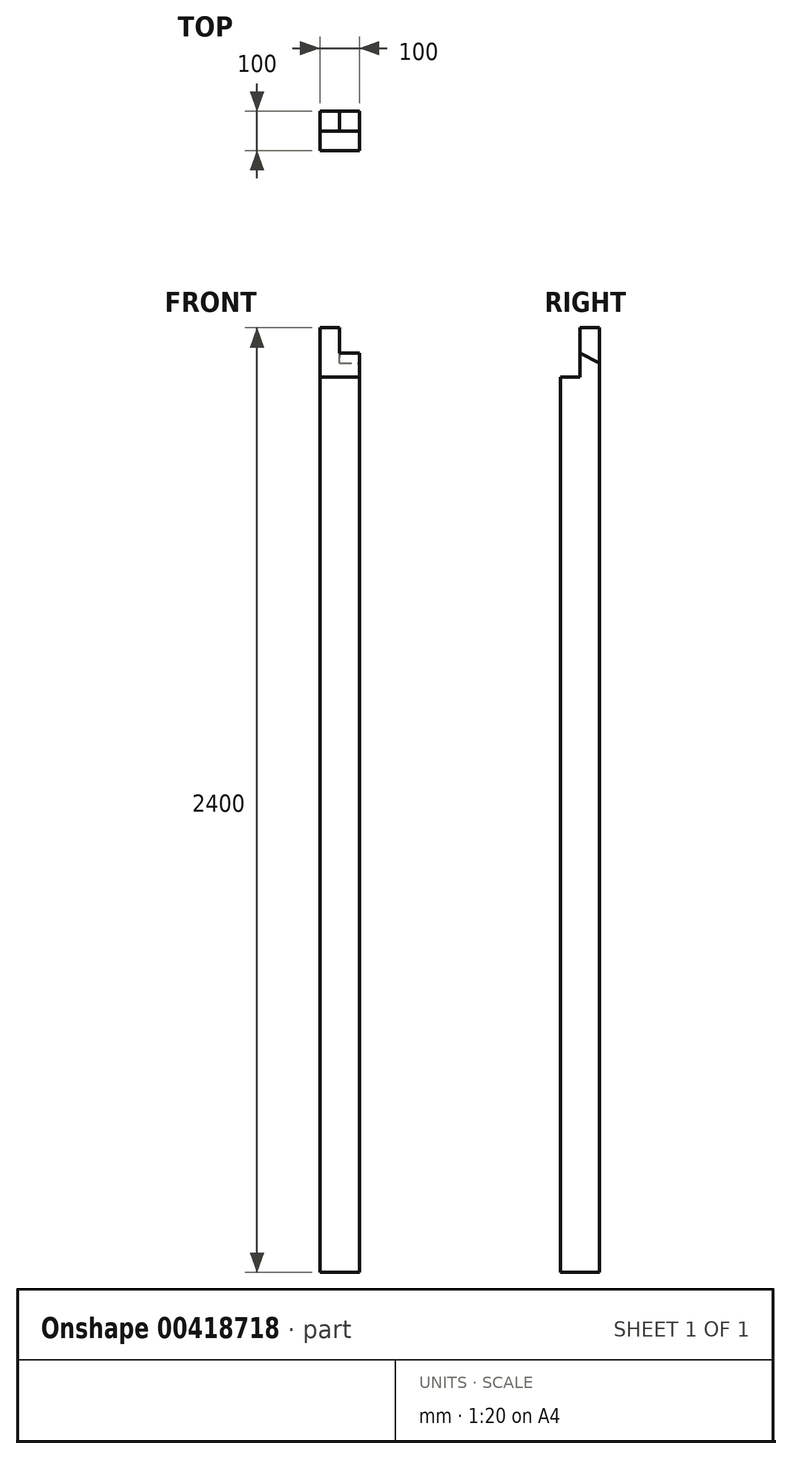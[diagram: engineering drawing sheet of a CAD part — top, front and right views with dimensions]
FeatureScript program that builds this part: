
annotation { "Feature Type Name" : "Feature", "Feature Type Description" : "" }
export const myFeature = defineFeature(function(context is Context, id is Id, definition is map)
    precondition{}
    {
        {
            var Q0;
            Q0=qCreatedBy(makeId("Top.planeOp"),FACE);
            var sketch = newSketch(context, id + "F0", { "sketchPlane" : qUnion([Q0])});
            skLineSegment(sketch, "E0.bottom", {"start": v(50, 50) * mm, "end": v(-50, 50) * mm});
            skLineSegment(sketch, "E0.top", {"start": v(50, -50) * mm, "end": v(-50, -50) * mm});
            skLineSegment(sketch, "E0.left", {"start": v(50, 50) * mm, "end": v(50, -50) * mm});
            skLineSegment(sketch, "E0.right", {"start": v(-50, 50) * mm, "end": v(-50, -50) * mm});
            skPoint(sketch, "E0.middle", {"position": v(0, 0) * mm});
            skSolve(sketch);
        }
        {
            var Q0;
            Q0=qSketchRegion(id+"F0",true);
            extrude(context, id + "F1", {"entities" : qUnion([Q0]), "depth" : 2400 * mm});
        }
        {
            var Q0;
            Q0=qCreatedBy(makeId("Right.planeOp"),FACE);
            var sketch = newSketch(context, id + "F2", { "sketchPlane" : qUnion([Q0])});
            skLineSegment(sketch, "E1.bottom", {"start": v(-50, 2400) * mm, "end": v(0, 2400) * mm});
            skLineSegment(sketch, "E1.top", {"start": v(-50, 2275) * mm, "end": v(0, 2275) * mm});
            skLineSegment(sketch, "E1.left", {"start": v(-50, 2400) * mm, "end": v(-50, 2275) * mm});
            skLineSegment(sketch, "E1.right", {"start": v(0, 2400) * mm, "end": v(0, 2275) * mm});
            skSolve(sketch);
        }
        {
            var Q0;
            Q0=qSketchRegion(id+"F2",true);
            extrude(context, id + "F3", {"entities" : qUnion([Q0]), "operationType" : NewBodyOperationType.REMOVE, "endBound" : BoundingType.UP_TO_NEXT, "oppositeDirection" : true, "depth" : 25 * mm, "hasSecondDirection" : true, "secondDirectionBound" : SecondDirectionBoundingType.UP_TO_NEXT, "secondDirectionOppositeDirection" : false, "secondDirectionDepth" : 25 * mm});
        }
        {
            var Q0;
            Q0=makeQuery(id+"F1.opExtrude","SWEPT_FACE",FACE,{"disambiguationData":[OSD([sQuery(id+"F0.wireOp",EDGE,"E0.left")])]});
            var sketch = newSketch(context, id + "F4", { "sketchPlane" : qUnion([Q0])});
            skLineSegment(sketch, "E2", {"start": v(50, 2400) * mm, "end": v(50, 2310.25) * mm});
            skLineSegment(sketch, "E3", {"start": v(50, 2310.25) * mm, "end": v(0, 2335.25) * mm});
            skLineSegment(sketch, "E4", {"start": v(0, 2335.25) * mm, "end": v(0, 2400) * mm});
            skLineSegment(sketch, "E5", {"start": v(50, 2400) * mm, "end": v(0, 2400) * mm});
            skSolve(sketch);
        }
        {
            var Q0;
            Q0=qSketchRegion(id+"F4",true);
            extrude(context, id + "F5", {"entities" : qUnion([Q0]), "operationType" : NewBodyOperationType.REMOVE, "oppositeDirection" : true, "depth" : 50 * mm});
        }
    });
